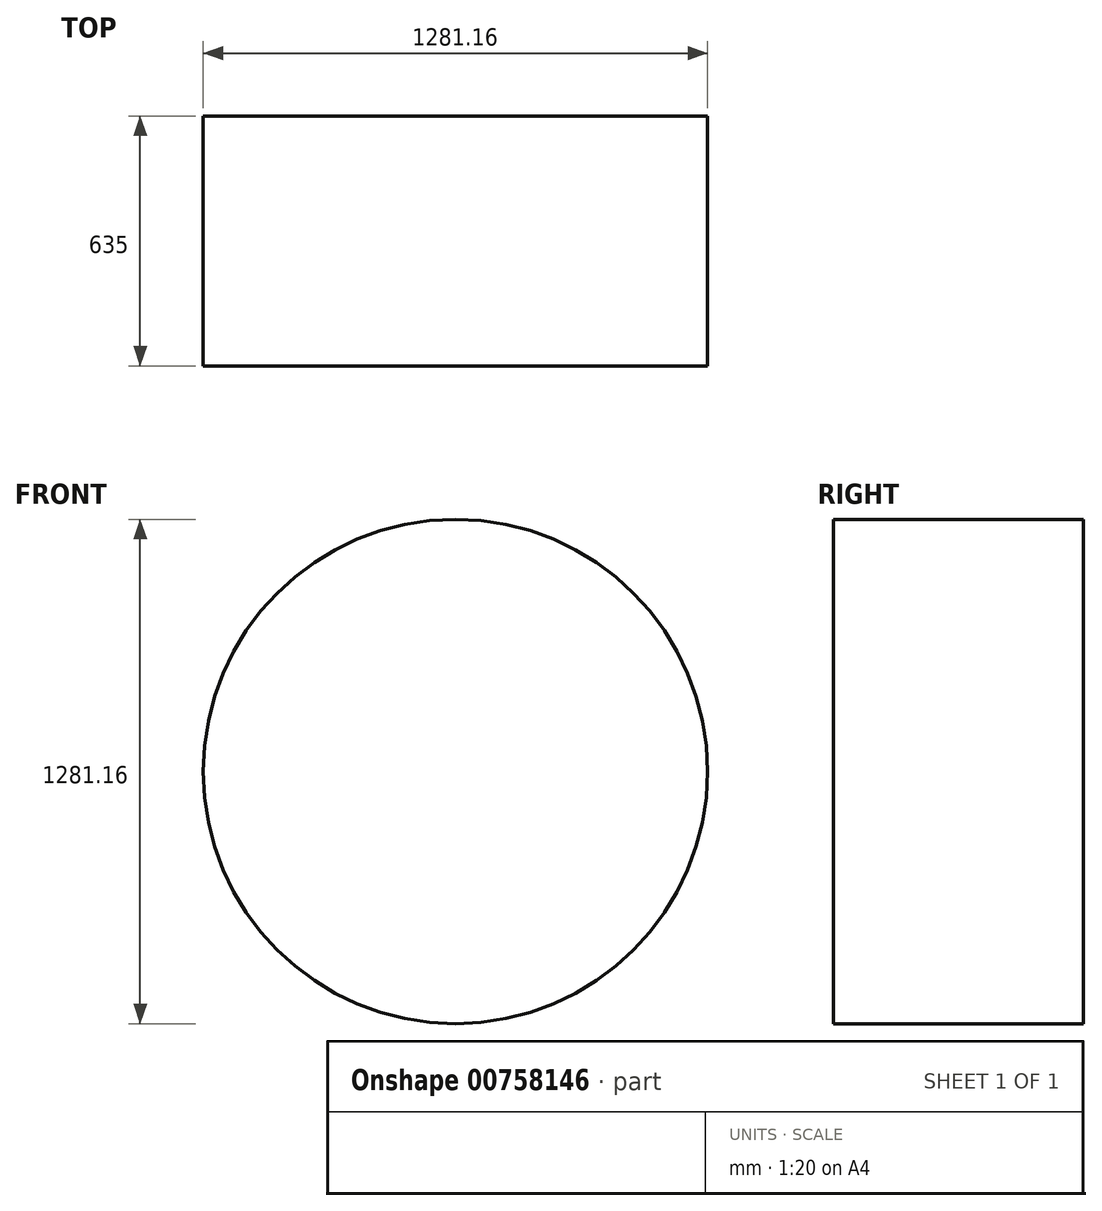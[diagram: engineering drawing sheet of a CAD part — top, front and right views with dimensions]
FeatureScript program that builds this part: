
annotation { "Feature Type Name" : "Feature", "Feature Type Description" : "" }
export const myFeature = defineFeature(function(context is Context, id is Id, definition is map)
    precondition{}
    {
        {
            var Q0;
            Q0=qCreatedBy(makeId("Front.planeOp"),FACE);
            var sketch = newSketch(context, id + "F0", { "sketchPlane" : qUnion([Q0])});
            skCircle(sketch, "E0", {"center": v(-1090.32, -685.87) * mm, "radius": 640.58 * mm});
            skSolve(sketch);
        }
        {
            var Q0;
            Q0=makeQuery(id+"F0.imprint","IMPRINT",FACE,{"disambiguationData":[TD([[makeQuery(id+"F0.imprint","IMPRINT",EDGE,{"derivedFrom":sQuery(id+"F0.wireOp",EDGE,"E0")}),1.0]])]});
            extrude(context, id + "F1", {"entities" : qUnion([Q0]), "depth" : 635 * mm, "offsetDistance" : 25.4 * mm});
        }
    });
